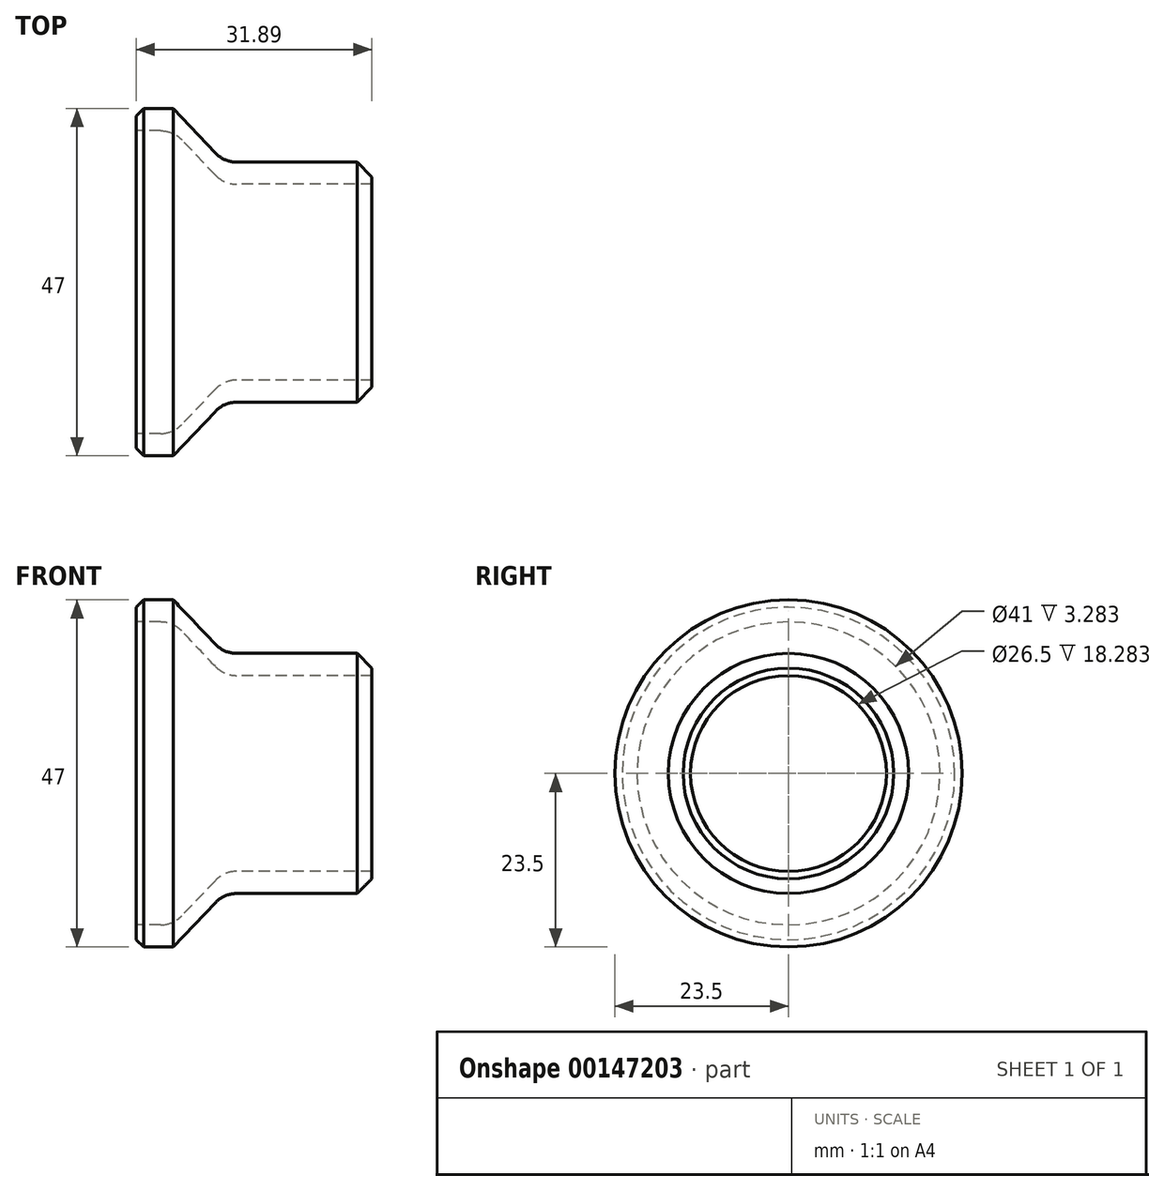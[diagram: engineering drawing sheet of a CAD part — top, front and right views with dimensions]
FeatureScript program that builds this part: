
annotation { "Feature Type Name" : "Feature", "Feature Type Description" : "" }
export const myFeature = defineFeature(function(context is Context, id is Id, definition is map)
    precondition{}
    {
        {
            var Q0;
            Q0=qCreatedBy(makeId("Front.planeOp"),FACE);
            var sketch = newSketch(context, id + "F0", { "sketchPlane" : qUnion([Q0])});
            skLineSegment(sketch, "E0", {"start": v(-5, 23.5) * mm, "end": v(0, 23.5) * mm});
            skLineSegment(sketch, "E1", {"start": v(0, 23.5) * mm, "end": v(6.89, 16.25) * mm});
            skLineSegment(sketch, "E2", {"start": v(6.89, 16.25) * mm, "end": v(26.89, 16.25) * mm});
            skLineSegment(sketch, "E3", {"start": v(26.89, 16.25) * mm, "end": v(26.89, 13.25) * mm});
            skLineSegment(sketch, "E4", {"start": v(26.89, 13.25) * mm, "end": v(6.89, 13.25) * mm});
            skLineSegment(sketch, "E5", {"start": v(6.89, 13.25) * mm, "end": v(0, 20.5) * mm});
            skLineSegment(sketch, "E6", {"start": v(0, 20.5) * mm, "end": v(-5, 20.5) * mm});
            skLineSegment(sketch, "E7", {"start": v(-5, 20.5) * mm, "end": v(-5, 23.5) * mm});
            skLineSegment(sketch, "E8", {"start": v(-28.06, 0) * mm, "end": v(47.4, 0) * mm, "construction": true});
            skSolve(sketch);
        }
        {
            var Q0;
            Q0=makeQuery(id+"F0.imprint","IMPRINT",FACE,{"disambiguationData":[TD([[makeQuery(id+"F0.imprint","IMPRINT",EDGE,{"derivedFrom":sQuery(id+"F0.wireOp",EDGE,"E0")}),-1.0]])]});
            var Q1;
            Q1=sQuery(id+"F0.wireOp",EDGE,"E8");
            revolve(context, id + "F1", {"entities" : qUnion([Q0]), "axis" : qUnion([Q1]), "revolveType" : RevolveType.FULL});
        }
        {
            var Q0;
            Q0=makeQuery(id+"F1.opRevolve","SWEPT_EDGE",EDGE,{"disambiguationData":[OSD([sQuery(id+"F0.wireOp",EDGE,"E0"),sQuery(id+"F0.wireOp",EDGE,"E7")])]});
            chamfer(context, id + "F2", {"entities" : qUnion([Q0]), "width" : 1 * mm, "tangentPropagation" : true});
        }
        {
            var Q0;
            Q0=makeQuery(id+"F1.opRevolve","SWEPT_EDGE",EDGE,{"disambiguationData":[OSD([sQuery(id+"F0.wireOp",EDGE,"E2"),sQuery(id+"F0.wireOp",EDGE,"E3")])]});
            chamfer(context, id + "F3", {"entities" : qUnion([Q0]), "width" : 2 * mm, "tangentPropagation" : true});
        }
        {
            var Q0;
            Q0=makeQuery(id+"F1.opRevolve","SWEPT_EDGE",EDGE,{"disambiguationData":[OSD([sQuery(id+"F0.wireOp",EDGE,"E1"),sQuery(id+"F0.wireOp",EDGE,"E2")])]});
            var Q1;
            Q1=makeQuery(id+"F1.opRevolve","SWEPT_EDGE",EDGE,{"disambiguationData":[OSD([sQuery(id+"F0.wireOp",EDGE,"E4"),sQuery(id+"F0.wireOp",EDGE,"E5")])]});
            var Q2;
            Q2=makeQuery(id+"F1.opRevolve","SWEPT_EDGE",EDGE,{"disambiguationData":[OSD([sQuery(id+"F0.wireOp",EDGE,"E5"),sQuery(id+"F0.wireOp",EDGE,"E6")])]});
            fillet(context, id + "F4", {"entities" : qUnion([Q0, Q1, Q2]), "radius" : 4 * mm, "tangentPropagation" : true, "allowEdgeOverflow" : false});
        }
    });
